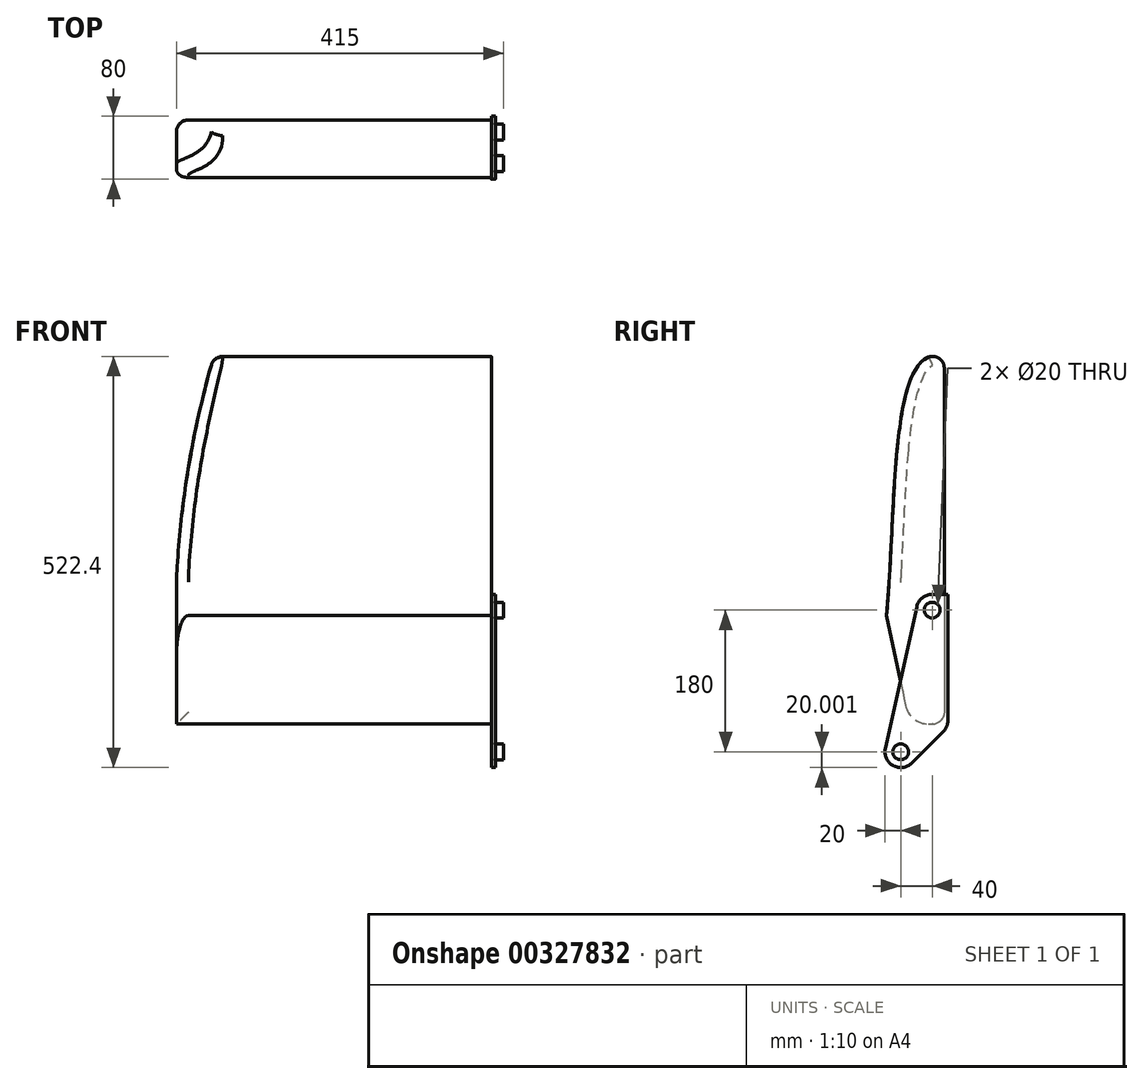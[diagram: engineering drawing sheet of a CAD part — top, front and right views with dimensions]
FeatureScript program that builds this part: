
annotation { "Feature Type Name" : "Feature", "Feature Type Description" : "" }
export const myFeature = defineFeature(function(context is Context, id is Id, definition is map)
    precondition{}
    {
        {
            var Q0;
            Q0=qCreatedBy(makeId("Right.planeOp"),FACE);
            var sketch = newSketch(context, id + "F0", { "sketchPlane" : qUnion([Q0])});
            skLineSegment(sketch, "E0.bottom", {"start": v(55.36, 617.15) * mm, "end": v(15.36, 617.15) * mm, "construction": true});
            skLineSegment(sketch, "E0.top", {"start": v(55.36, 0) * mm, "end": v(15.36, 0) * mm, "construction": true});
            skLineSegment(sketch, "E0.left", {"start": v(55.36, 617.15) * mm, "end": v(55.36, 155) * mm});
            skLineSegment(sketch, "E0.right", {"start": v(15.36, 617.15) * mm, "end": v(15.36, 259.02) * mm, "construction": true});
            skCircle(sketch, "E1", {"center": v(35.36, 275) * mm, "radius": 10 * mm, "construction": true});
            skLineSegment(sketch, "E2", {"start": v(-5.14, 496.97) * mm, "end": v(-21.32, 319.13) * mm});
            skFitSpline(sketch, "E3.trimOffspring", {"points": [v(55.39, 17.13) * mm, v(-22.28, 106.65) * mm, v(-17.2, 301.54) * mm, v(15.39, 599.12) * mm, v(55.39, 617.13) * mm], "startDerivative": vector(-459.62, -212.02) * mm, "endDerivative": vector(346.5, -252.93) * mm});
            skPoint(sketch, "E4.3.internal.orphan", {"position": v(15.36, 582) * mm});
            skPoint(sketch, "E5.center.orphan", {"position": v(35.36, 25) * mm});
            skLineSegment(sketch, "E6", {"start": v(6.47, 155) * mm, "end": v(55.36, 155) * mm, "construction": true});
            skArc(sketch, "E7.filletArc", {"start": v(-32.29, 198.61) * mm, "mid": v(-22.35, 168.41) * mm, "end": v(6.47, 155) * mm, "construction": true});
            skLineSegment(sketch, "E8", {"start": v(-20.44, 304.23) * mm, "end": v(6.17, 178.78) * mm});
            skArc(sketch, "E9.filletArc", {"start": v(-21.32, 319.13) * mm, "mid": v(-21.44, 311.65) * mm, "end": v(-20.44, 304.23) * mm});
            skLineSegment(sketch, "E10", {"start": v(35.52, 155) * mm, "end": v(55.36, 155) * mm});
            skPoint(sketch, "E11.visualSharp", {"position": v(11.22, 155) * mm});
            skArc(sketch, "E11.filletArc", {"start": v(6.17, 178.78) * mm, "mid": v(16.64, 161.69) * mm, "end": v(35.52, 155) * mm});
            skSolve(sketch);
        }
        {
            var Q0;
            Q0=makeQuery(id+"F0.imprint","IMPRINT",FACE,{"disambiguationData":[TD([[makeQuery(id+"F0.imprint","IMPRINT",EDGE,{"derivedFrom":sQuery(id+"F0.wireOp",EDGE,"E0.left")}),-1.0]])]});
            extrude(context, id + "F1", {"entities" : qUnion([Q0]), "endBound" : BoundingType.SYMMETRIC, "depth" : 400 * mm});
        }
        {
            var Q0;
            Q0=makeQuery(id+"F1.opExtrude","CAP_FACE",FACE,{"disambiguationData":[OSD([sQuery(id+"F0.wireOp",EDGE,"E0.left"),sQuery(id+"F0.wireOp",EDGE,"E4")])],"isStart":false});
            var sketch = newSketch(context, id + "F2", { "sketchPlane" : qUnion([Q0])});
            skCircle(sketch, "E12", {"center": v(40, 299.68) * mm, "radius": 10 * mm});
            skCircle(sketch, "E13", {"center": v(0, 119.68) * mm, "radius": 10 * mm});
            skLineSegment(sketch, "E14", {"start": v(0, 119.68) * mm, "end": v(40, 119.68) * mm, "construction": true});
            skLineSegment(sketch, "E15", {"start": v(40, 119.68) * mm, "end": v(40, 299.68) * mm, "construction": true});
            skSolve(sketch);
        }
        {
            var Q0;
            Q0=qCreatedBy(makeId("Front.planeOp"),FACE);
            var sketch = newSketch(context, id + "F3", { "sketchPlane" : qUnion([Q0])});
            skArc(sketch, "E16", {"start": v(-148.5, 636.23) * mm, "mid": v(-184.24, 485.04) * mm, "end": v(-200.49, 330.55) * mm});
            skLineSegment(sketch, "E17", {"start": v(0, 636.23) * mm, "end": v(0, 135.57) * mm, "construction": true});
            skArc(sketch, "E18.MirrorCS", {"start": v(148.5, 636.23) * mm, "mid": v(184.24, 485.04) * mm, "end": v(200.49, 330.55) * mm});
            skLineSegment(sketch, "E19", {"start": v(-148.5, 636.23) * mm, "end": v(-242.8, 636.23) * mm});
            skLineSegment(sketch, "E20", {"start": v(-242.8, 636.23) * mm, "end": v(-242.8, 330.55) * mm});
            skLineSegment(sketch, "E21", {"start": v(-242.8, 330.55) * mm, "end": v(-200.49, 330.55) * mm});
            skSolve(sketch);
        }
        {
            var Q0;
            Q0=makeQuery(id+"F3.imprint","IMPRINT",FACE,{"disambiguationData":[TD([[makeQuery(id+"F3.imprint","IMPRINT",EDGE,{"derivedFrom":sQuery(id+"F3.wireOp",EDGE,"E16")}),-1.0]])]});
            var Q1;
            Q1=makeQuery(id+"FlFj3GTT4LpDJiT_4.1.F3.imprint","IMPRINT",FACE,{"disambiguationData":[TD([[makeQuery(id+"FlFj3GTT4LpDJiT_4.1.F3.imprint","IMPRINT",EDGE,{"derivedFrom":sQuery(id+"FlFj3GTT4LpDJiT_4.1.F3.wireOp",EDGE,"E16")}),-1.0]])]});
            extrude(context, id + "F4", {"entities" : qUnion([Q0, Q1]), "operationType" : NewBodyOperationType.REMOVE, "endBound" : BoundingType.SYMMETRIC, "oppositeDirection" : true, "depth" : 200 * mm, "offsetDistance" : 25 * mm});
        }
        {
            var Q0;
            Q0=makeQuery(id+"F2.imprint","IMPRINT",FACE,{"disambiguationData":[TD([[makeQuery(id+"F2.imprint","IMPRINT",EDGE,{"derivedFrom":sQuery(id+"F2.wireOp",EDGE,"E12")}),1.0]])]});
            var Q1;
            Q1=makeQuery(id+"F2.imprint","IMPRINT",FACE,{"disambiguationData":[TD([[makeQuery(id+"F2.imprint","IMPRINT",EDGE,{"derivedFrom":sQuery(id+"F2.wireOp",EDGE,"E13")}),1.0]])]});
            extrude(context, id + "F5", {"entities" : qUnion([Q0, Q1]), "operationType" : NewBodyOperationType.ADD, "depth" : 15 * mm, "offsetDistance" : 25 * mm});
        }
        {
            var Q0;
            Q0=makeQuery(id+"F2.imprint","IMPRINT",FACE,{"disambiguationData":[TD([[makeQuery(id+"F2.imprint","IMPRINT",EDGE,{"derivedFrom":sQuery(id+"F2.wireOp",EDGE,"E12")}),-1.0]])]});
            var sketch = newSketch(context, id + "F6", { "sketchPlane" : qUnion([Q0])});
            skLineSegment(sketch, "E22", {"start": v(20.48, 304.02) * mm, "end": v(-19.52, 124.02) * mm});
            skLineSegment(sketch, "E23", {"start": v(60, 319.68) * mm, "end": v(60, 159.68) * mm});
            skLineSegment(sketch, "E24", {"start": v(54.14, 145.54) * mm, "end": v(14.14, 105.54) * mm});
            skArc(sketch, "E25", {"start": v(40, 319.68) * mm, "mid": v(27.49, 315.28) * mm, "end": v(20.48, 304.02) * mm});
            skArc(sketch, "E26", {"start": v(-19.52, 124.02) * mm, "mid": v(-9.62, 102.15) * mm, "end": v(14.14, 105.54) * mm});
            skPoint(sketch, "E27.visualSharp", {"position": v(60, 151.4) * mm});
            skArc(sketch, "E27.filletArc", {"start": v(54.14, 145.54) * mm, "mid": v(58.48, 152.03) * mm, "end": v(60, 159.68) * mm});
            skLineSegment(sketch, "E28", {"start": v(40, 319.68) * mm, "end": v(60, 319.68) * mm});
            skPoint(sketch, "E28.startSnap0", {"position": v(40, 319.68) * mm});
            skCircle(sketch, "E29.0", {"center": v(0, 119.68) * mm, "radius": 10 * mm});
            skCircle(sketch, "E29.1", {"center": v(40, 299.68) * mm, "radius": 10 * mm});
            skSolve(sketch);
        }
        {
            var Q0;
            {var subQ4=sQuery(id+"F6.wireOp",EDGE,"E25");Q0=makeQuery(id+"F6.imprint","IMPRINT",FACE,{"disambiguationData":[TD([[makeQuery(id+"F6.imprint","IMPRINT",EDGE,{"derivedFrom":subQ4}),1.0]])]});}
            var Q1;
            Q1=makeQuery(id+"F6.imprint","IMPRINT",FACE,{"disambiguationData":[TD([[makeQuery(id+"F6.imprint","IMPRINT",EDGE,{"derivedFrom":sQuery(id+"F6.wireOp",EDGE,"E24")}),-1.0]])]});
            extrude(context, id + "F7", {"entities" : qUnion([Q0, Q1]), "depth" : 5 * mm, "offsetDistance" : 25 * mm});
        }
        {
            var Q0;
            Q0=makeQuery(id+"F4.boolean.opBoolean","INTERSECT",EDGE,{"derivedFrom":[makeQuery(id+"F1.opExtrude","CAP_FACE",FACE,{"disambiguationData":[OSD([sQuery(id+"F0.wireOp",EDGE,"E0.left"),sQuery(id+"F0.wireOp",EDGE,"E2"),sQuery(id+"F0.wireOp",EDGE,"E3.trimOffspring"),sQuery(id+"F0.wireOp",EDGE,"E8"),sQuery(id+"F0.wireOp",EDGE,"E9.filletArc"),sQuery(id+"F0.wireOp",EDGE,"E10"),sQuery(id+"F0.wireOp",EDGE,"E11.filletArc")])],"isStart":false}),makeQuery(id+"F4.opExtrude","SWEPT_FACE",FACE,{"disambiguationData":[OSD([sQuery(id+"FlFj3GTT4LpDJiT_4.1.F3.wireOp",EDGE,"E16")])]})]});
            var Q1;
            Q1=makeQuery(id+"F4.boolean.opBoolean","INTERSECT",EDGE,{"derivedFrom":[makeQuery(id+"F1.opExtrude","CAP_FACE",FACE,{"disambiguationData":[OSD([sQuery(id+"F0.wireOp",EDGE,"E0.left"),sQuery(id+"F0.wireOp",EDGE,"E2"),sQuery(id+"F0.wireOp",EDGE,"E3.trimOffspring"),sQuery(id+"F0.wireOp",EDGE,"E8"),sQuery(id+"F0.wireOp",EDGE,"E9.filletArc"),sQuery(id+"F0.wireOp",EDGE,"E10"),sQuery(id+"F0.wireOp",EDGE,"E11.filletArc")])],"isStart":true}),makeQuery(id+"F4.opExtrude","SWEPT_FACE",FACE,{"disambiguationData":[OSD([sQuery(id+"F3.wireOp",EDGE,"E16")])]})]});
            fillet(context, id + "F8", {"entities" : qUnion([Q0, Q1]), "radius" : 250 * mm, "allowEdgeOverflow" : false});
        }
        {
            var Q0;
            Q0=makeQuery(id+"F4.boolean.opBoolean","COPY",FACE,{"derivedFrom":makeQuery(id+"F4.opExtrude","SWEPT_FACE",FACE,{"disambiguationData":[OSD([sQuery(id+"F3.wireOp",EDGE,"E16")])]})});
            var Q1;
            Q1=makeQuery(id+"F4.boolean.opBoolean","COPY",FACE,{"derivedFrom":makeQuery(id+"F4.opExtrude","SWEPT_FACE",FACE,{"disambiguationData":[OSD([sQuery(id+"FlFj3GTT4LpDJiT_4.1.F3.wireOp",EDGE,"E16")])]})});
            var Q2;
            Q2=makeQuery(id+"F1.opExtrude","SWEPT_EDGE",EDGE,{"disambiguationData":[OSD([sQuery(id+"F0.wireOp",EDGE,"E0.left"),sQuery(id+"F0.wireOp",EDGE,"E3.trimOffspring")])]});
            var Q3;
            Q3=makeQuery(id+"F1.opExtrude","SWEPT_EDGE",EDGE,{"disambiguationData":[OSD([sQuery(id+"F0.wireOp",EDGE,"E0.left"),sQuery(id+"F0.wireOp",EDGE,"E10")])]});
            fillet(context, id + "F9", {"entities" : qUnion([Q0, Q1, Q2, Q3]), "radius" : 15 * mm, "tangentPropagation" : true, "allowEdgeOverflow" : false});
        }
    });
